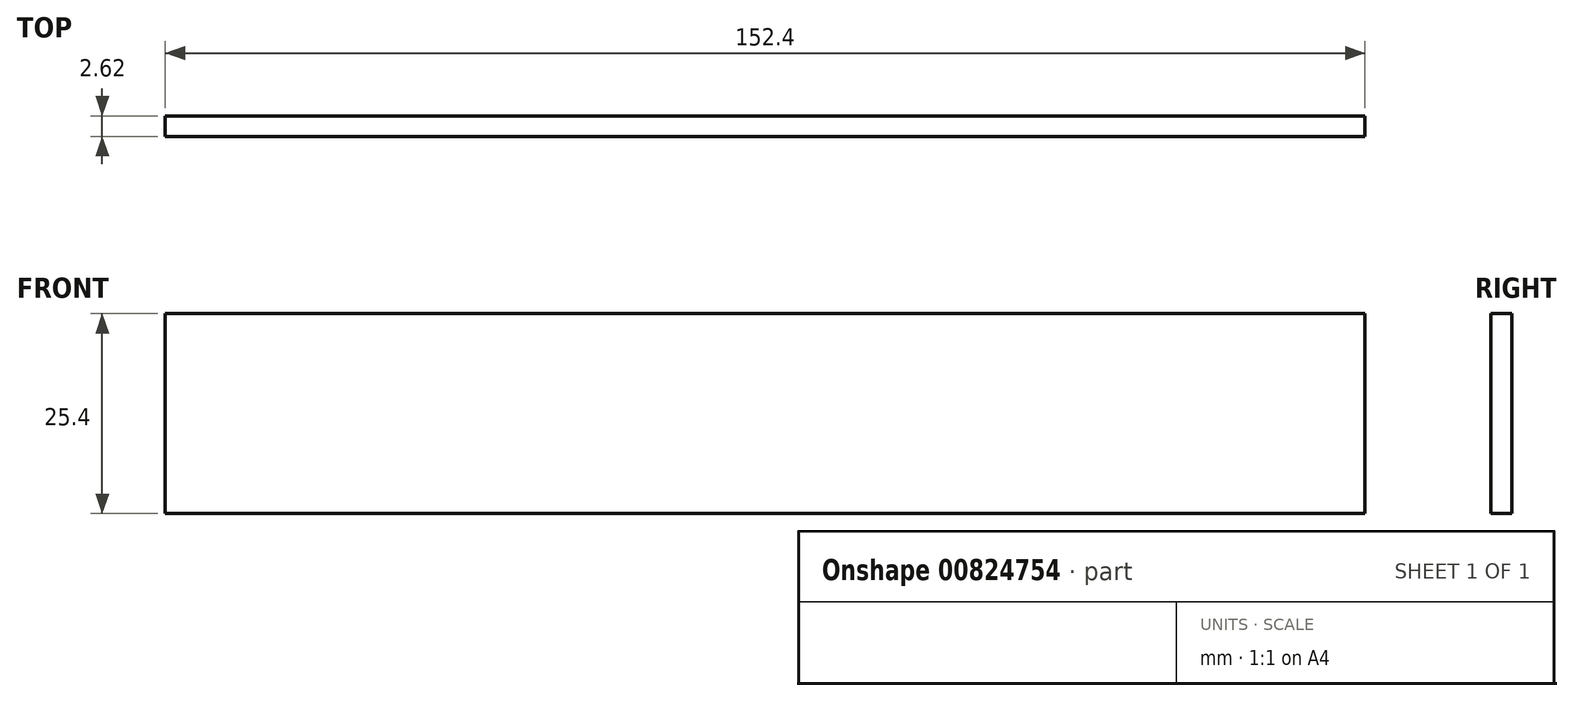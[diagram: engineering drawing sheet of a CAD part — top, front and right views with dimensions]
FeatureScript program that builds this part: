
annotation { "Feature Type Name" : "Feature", "Feature Type Description" : "" }
export const myFeature = defineFeature(function(context is Context, id is Id, definition is map)
    precondition{}
    {
        {
            var Q0;
            Q0=qCreatedBy(makeId("Front.planeOp"),FACE);
            var sketch = newSketch(context, id + "F0", { "sketchPlane" : qUnion([Q0])});
            skLineSegment(sketch, "E0.bottom", {"start": v(0, 0) * mm, "end": v(152.4, 0) * mm});
            skLineSegment(sketch, "E0.top", {"start": v(0, 25.4) * mm, "end": v(152.4, 25.4) * mm});
            skLineSegment(sketch, "E0.left", {"start": v(0, 0) * mm, "end": v(0, 25.4) * mm});
            skLineSegment(sketch, "E0.right", {"start": v(152.4, 0) * mm, "end": v(152.4, 25.4) * mm});
            skSolve(sketch);
        }
        {
            var Q0;
            Q0=makeQuery(id+"F0.imprint","IMPRINT",FACE,{"disambiguationData":[TD([[makeQuery(id+"F0.imprint","IMPRINT",EDGE,{"derivedFrom":sQuery(id+"F0.wireOp",EDGE,"E0.bottom")}),1.0]])]});
            extrude(context, id + "F1", {"entities" : qUnion([Q0]), "depth" : 2.62 * mm, "offsetDistance" : 25.4 * mm});
        }
    });
